# Revit family: QF_BPRO_BLT 620 KBRUH-F_573319
name_source: partatom
category: Sonderausstattung
revit_build: Autodesk Revit 2018 (Build: 20190510_1515(x64)
units: mm (PartAtom-declared; Revit-internal decimal feet)

## family parameters
Arbeitsebenenbasiert = Nein
Beim Laden mit Abzugskörper schneiden = Nein
Bemaßung runder Anschluss = Durchmesser verwenden
Gemeinsam genutzt = Nein
Immer vertikal = Ja
Raumberechnungspunkt = Nein
Teiletyp = Normal

## types (1)
- BLT 620 KBUH-F
    Artikel Nummer = 573319
    Beschreibung = B.PROTHERM Kunststoff, BLT 620 KBRUH-F mit Kondensat-Rinne
Farbe Beschlagteile grau
B.PROTHERM Speisentransportbehälter aus Kunststoff,
umluftbeheizt, mit digitalem Temperaturregler zur gradweisen REgelung der Temperatur im Innenraum von  +40 °C bis +85°C,
fahrbar mit Rollen gemäß DIN 18867-8 aus Kunststoff, 4 Lenkrollen, davon 2 mit Feststeller,
mit Flügeltür
    Beschreibung durch Hersteller analog Leistungsverzeichniskurztext = Abmessungen

Länge:				747 mm
Breite:			440 mm
Höhe:			831 mm


Ausführung


Der Speisentransportbehälter wird im Thermoform-Verfahren hergestellt und besteht aus hochwertigem, physiologisch unbedenklichem und lebensmittelbeständigem Polypropylen. 
Der doppelwandige Kunststoffbehälter und die Tür sind mit PUR-Schaum temperaturisolierend ausgeschäumt. Innen- und Außenbehälter sind dicht verschweißt. Die Kunststoffoberfläche ist glatt und porenfrei.

Längsseitig am Korpus befinden sich in Mulden vertieft Edelstahltragebügel mit ergonomisch geformten Kunststoff-Tragegriffen. Die Edelstahltragebügel ermöglichen auch bei einer starken Beanspruchung einen verschleißarmen Gebrauch.

Der Behälter ist mit einer um 270° schwenkbaren, bei Bedarf abnehmbaren Flügeltür ausgestattet. Das patentierte Türscharnier gewährleistet, dass die Tür nur in einer fest definierten Position abgenommen werden kann. Dadurch werden ein unbeabsichtigtes  Aushängen der Tür und damit Verletzungsgefahr vermieden. 
Die Tür wird über einen längsseitig im Behälter liegenden Edelstahl-Spannverschluss, der in der Tür einrastet, verschlossen.
Auf der Tür ist eine Aufnahmevorrichtung für Beschriftungskarten integriert zur Kennzeichnung der sich im Behälter befindlichen Speisen. 

Die Behälteroberseite ist mit vier angeschraubten Stapelecken versehen. Alle B.PROTHERM-Behälter sind untereinander stapelbar.

Der Behälter ist mit einem Fahrgestell, bestehend aus einer Bodenplatte aus Polyethylen inklusive Kondensat-Auffangrinne ausgestattet. Die Kondesat-Auffangrinne dient der Vermeidung von Rutsch- und Verletzungsgefahr.
An der stabilen Bodenplatte sind 4 Lenkrollen aus Kunststoff, rostfrei gem. DIN 18867-8, davon 2 mit Feststeller, Rollendurchmesser 125 mm befestigt. 

Alle Verschleißteile (Stapelecken, Griffe, Türscharnier und Türverschluss) sind im Servicefall einfach austauschbar. Alle versenkten Schrauben sind aus Hygienegründen mit Kunststoffstopfen abgedeckt.

Die Bestückung des BLT 620 KBRUH erfolgt von vorne. Der Innenkorpus des Behälters ist mit 12 Paar angeformten Auflagesicken im Abstand von 39 mm zur Aufnahme von Gastronorm-Behältern versehen.

Das Umluftheizmodul ist fest in der Innenseite der Flügeltür integriert. Im oberen Bereich der Tür befindet sich der Elektroanschluss mit Netzsteckerkupplung, welcher durch einen Spezial-Drehverschluss spritzwasserfest verschlossen werden kann. 
Daneben befindet sich der digitale Regler mit LED-Display. 
Die Temperatur im Innern des Behälters ist gradweise regelbar von +40°C bis +85°C, für ein besonders schonendes und appetitliches Warmhalten der Speisen. 
Im Full-Power-Modus wird eine Temperatur von ca. +90°C erreicht. Die Ist-Temperatur im Inneren des Behälters wird auf dem LED-Display angezeigt.
Die Heizung ist mit einem integrierten Überhitzungsschutz ausgestattet, um ein Weitergaren der Speisen zu verhindern. 
Das Netzanschlusskabel ist dem Behälter lose beigefügt.


Zubehör/ Optionen

•	verschiedene Transportwagen und -Rollis siehe Gesamt-Preisliste
•	Eutektische Platte -3°C (Art. Nr. 568136)
•	Eutektische Plartte -12°C (Art. Nr. 573332)
•	Einschubrahmen zur Unterteilung von GN-Behältern mit max. Tiefe 150 mm 
(Art. Nr. 564352)
•	GN-Stege zum variablen Einsetzen von GN-Behältern der Größe GN 1/4, GN 1/6, GN 1/9 in den Einschubrahmen (ST 3 Art. Nr. 550650, ST 5 Art. Nr. 550651)
•	Menükarten incl. Zubehör siehe Gesamt-Preisliste
 
Technische Daten

Werkstoff:	Polypropylen (PP), Polyethylen (PE), Polyamid (PA), Edelstahl
Temperatur-
beständigkeit.	-25°C  bis +100°C
Isoliermaterial:	PUR-Schaum - FCKW-frei 
Sicken:	                        12 Paar Auflagesicken, Abstand 39 mm
Kapazität:	2 x GN 1/1-200
Aufheizzeit:	im Full-Power-Modus im leeren Behälter wird in 45 Min. eine Temperatur von ca. 75°C erreicht
Gewicht:    	28,01 kg 
Elektr. Anschluss:	220-240 V AC/ 50 Hz/200 Watt 
Emissionen:	Der arbeitsplatzbezogene Schallpegel des Geräts ist kleiner als 70 dB(A)


Besonderheit

•	Schutz gegen Spritzwasser IP X4
•	VDE-GS geprüft
•	recyclebar 
•	Fahrbarer Speisentransportbehälter
•	Gradweise Temperaturregelung von +40°C bis +85°C
•	Temperaturanzeige
•	Heizung mit integriertem Überhitzungsschutz
•	Patentiertes Türscharnier (nur in fest definierter Position aushängbar)
•	Griffmulde links oben in der Tür für leichtes Umsetzen und optimales Handling des Behälters
•	Mit Kondensat-Auffangrinne zur Vermeidung von Rutsch- und Verletzungsgefahr



Fabrikat

Hersteller:    B.PRO
Modell:	BLT 620 KBRUH-F mit 
	Kondensat-Rinne
	B.PROTHERM
Best.Nr.	573 319
    Beschreibung durch Hersteller analog Leistungsverzeichnislangtext = Abmessungen

Länge:				747 mm
Breite:			440 mm
Höhe:			831 mm


Ausführung


Der Speisentransportbehälter wird im Thermoform-Verfahren hergestellt und besteht aus hochwertigem, physiologisch unbedenklichem und lebensmittelbeständigem Polypropylen. 
Der doppelwandige Kunststoffbehälter und die Tür sind mit PUR-Schaum temperaturisolierend ausgeschäumt. Innen- und Außenbehälter sind dicht verschweißt. Die Kunststoffoberfläche ist glatt und porenfrei.

Längsseitig am Korpus befinden sich in Mulden vertieft Edelstahltragebügel mit ergonomisch geformten Kunststoff-Tragegriffen. Die Edelstahltragebügel ermöglichen auch bei einer starken Beanspruchung einen verschleißarmen Gebrauch.

Der Behälter ist mit einer um 270° schwenkbaren, bei Bedarf abnehmbaren Flügeltür ausgestattet. Das patentierte Türscharnier gewährleistet, dass die Tür nur in einer fest definierten Position abgenommen werden kann. Dadurch werden ein unbeabsichtigtes  Aushängen der Tür und damit Verletzungsgefahr vermieden. 
Die Tür wird über einen längsseitig im Behälter liegenden Edelstahl-Spannverschluss, der in der Tür einrastet, verschlossen.
Auf der Tür ist eine Aufnahmevorrichtung für Beschriftungskarten integriert zur Kennzeichnung der sich im Behälter befindlichen Speisen. 

Die Behälteroberseite ist mit vier angeschraubten Stapelecken versehen. Alle B.PROTHERM-Behälter sind untereinander stapelbar.

Der Behälter ist mit einem Fahrgestell, bestehend aus einer Bodenplatte aus Polyethylen inklusive Kondensat-Auffangrinne ausgestattet. Die Kondesat-Auffangrinne dient der Vermeidung von Rutsch- und Verletzungsgefahr.
An der stabilen Bodenplatte sind 4 Lenkrollen aus Kunststoff, rostfrei gem. DIN 18867-8, davon 2 mit Feststeller, Rollendurchmesser 125 mm befestigt. 

Alle Verschleißteile (Stapelecken, Griffe, Türscharnier und Türverschluss) sind im Servicefall einfach austauschbar. Alle versenkten Schrauben sind aus Hygienegründen mit Kunststoffstopfen abgedeckt.

Die Bestückung des BLT 620 KBRUH erfolgt von vorne. Der Innenkorpus des Behälters ist mit 12 Paar angeformten Auflagesicken im Abstand von 39 mm zur Aufnahme von Gastronorm-Behältern versehen.

Das Umluftheizmodul ist fest in der Innenseite der Flügeltür integriert. Im oberen Bereich der Tür befindet sich der Elektroanschluss mit Netzsteckerkupplung, welcher durch einen Spezial-Drehverschluss spritzwasserfest verschlossen werden kann. 
Daneben befindet sich der digitale Regler mit LED-Display. 
Die Temperatur im Innern des Behälters ist gradweise regelbar von +40°C bis +85°C, für ein besonders schonendes und appetitliches Warmhalten der Speisen. 
Im Full-Power-Modus wird eine Temperatur von ca. +90°C erreicht. Die Ist-Temperatur im Inneren des Behälters wird auf dem LED-Display angezeigt.
Die Heizung ist mit einem integrierten Überhitzungsschutz ausgestattet, um ein Weitergaren der Speisen zu verhindern. 
Das Netzanschlusskabel ist dem Behälter lose beigefügt.


Zubehör/ Optionen

•	verschiedene Transportwagen und -Rollis siehe Gesamt-Preisliste
•	Eutektische Platte -3°C (Art. Nr. 568136)
•	Eutektische Plartte -12°C (Art. Nr. 573332)
•	Einschubrahmen zur Unterteilung von GN-Behältern mit max. Tiefe 150 mm 
(Art. Nr. 564352)
•	GN-Stege zum variablen Einsetzen von GN-Behältern der Größe GN 1/4, GN 1/6, GN 1/9 in den Einschubrahmen (ST 3 Art. Nr. 550650, ST 5 Art. Nr. 550651)
•	Menükarten incl. Zubehör siehe Gesamt-Preisliste
 
Technische Daten

Werkstoff:	Polypropylen (PP), Polyethylen (PE), Polyamid (PA), Edelstahl
Temperatur-
beständigkeit.	-25°C  bis +100°C
Isoliermaterial:	PUR-Schaum - FCKW-frei 
Sicken:	                        12 Paar Auflagesicken, Abstand 39 mm
Kapazität:	2 x GN 1/1-200
Aufheizzeit:	im Full-Power-Modus im leeren Behälter wird in 45 Min. eine Temperatur von ca. 75°C erreicht
Gewicht:    	28,01 kg 
Elektr. Anschluss:	220-240 V AC/ 50 Hz/200 Watt 
Emissionen:	Der arbeitsplatzbezogene Schallpegel des Geräts ist kleiner als 70 dB(A)


Besonderheit

•	Schutz gegen Spritzwasser IP X4
•	VDE-GS geprüft
•	recyclebar 
•	Fahrbarer Speisentransportbehälter
•	Gradweise Temperaturregelung von +40°C bis +85°C
•	Temperaturanzeige
•	Heizung mit integriertem Überhitzungsschutz
•	Patentiertes Türscharnier (nur in fest definierter Position aushängbar)
•	Griffmulde links oben in der Tür für leichtes Umsetzen und optimales Handling des Behälters
•	Mit Kondensat-Auffangrinne zur Vermeidung von Rutsch- und Verletzungsgefahr



Fabrikat

Hersteller:    B.PRO
Modell:	BLT 620 KBRUH-F mit 
	Kondensat-Rinne
	B.PROTHERM
Best.Nr.	573 319
    CE Kennzeichnung = Ja
    Elektrische leistung = 200 W
    Frequenz = 50 Hz
    Gerätegewicht Netto = 28.00 kg
    Großküchengerätezuordnung = Ja
    Hauptschalter integriert = Nein
    Hersteller = B.PRO GmbH
    Höhe = 831 mm  [stored 2.72638 ft]
    Internetadresse Gerätehersteller = https://www.bpro-solutions.com
    Internetadresse für Ersatzteilliste = https://www.bpro-solutions.com
    Kosten = 1603.7 $
    Länge Gerätebreite = 440 mm  [stored 1.44357 ft]
    Material = QF_Plastic-Grey-Matt
    Material Anbauteile = QF_Plastic-Black-Matt
    Material Metall glänzend = QF_Metal-Stainless-Steel_glossy
    Material Sockel = QF_Plastic-Black-Matt
    Modell = BLT 620 KBUH-F
    Schalldruckpegel = < 70 dB(A)
    Sockelhöhe = 174 mm
    Spannung = 240 V
    Stecker System = Schuko Stecker
    Tiefe = 747 mm
    Typenkommentare = B.PROTHERM Kunststoff, BLT 620 KBRUH-F mit Kondensat-Rinne, Farbe Beschlagteile grau
    URL = https://www.bpro-solutions.com
    Warnhinweise = Ausführliche Gefahrenhinweise entnehmen Sie der Betriebsanleitung.
    Zubehör = Nein
    Zuleitung zum Gerät im Lieferumfang = Ja

note: [stored X ft] marks values corroborated as IEEE doubles in the binary element streams (Revit-internal decimal feet)
